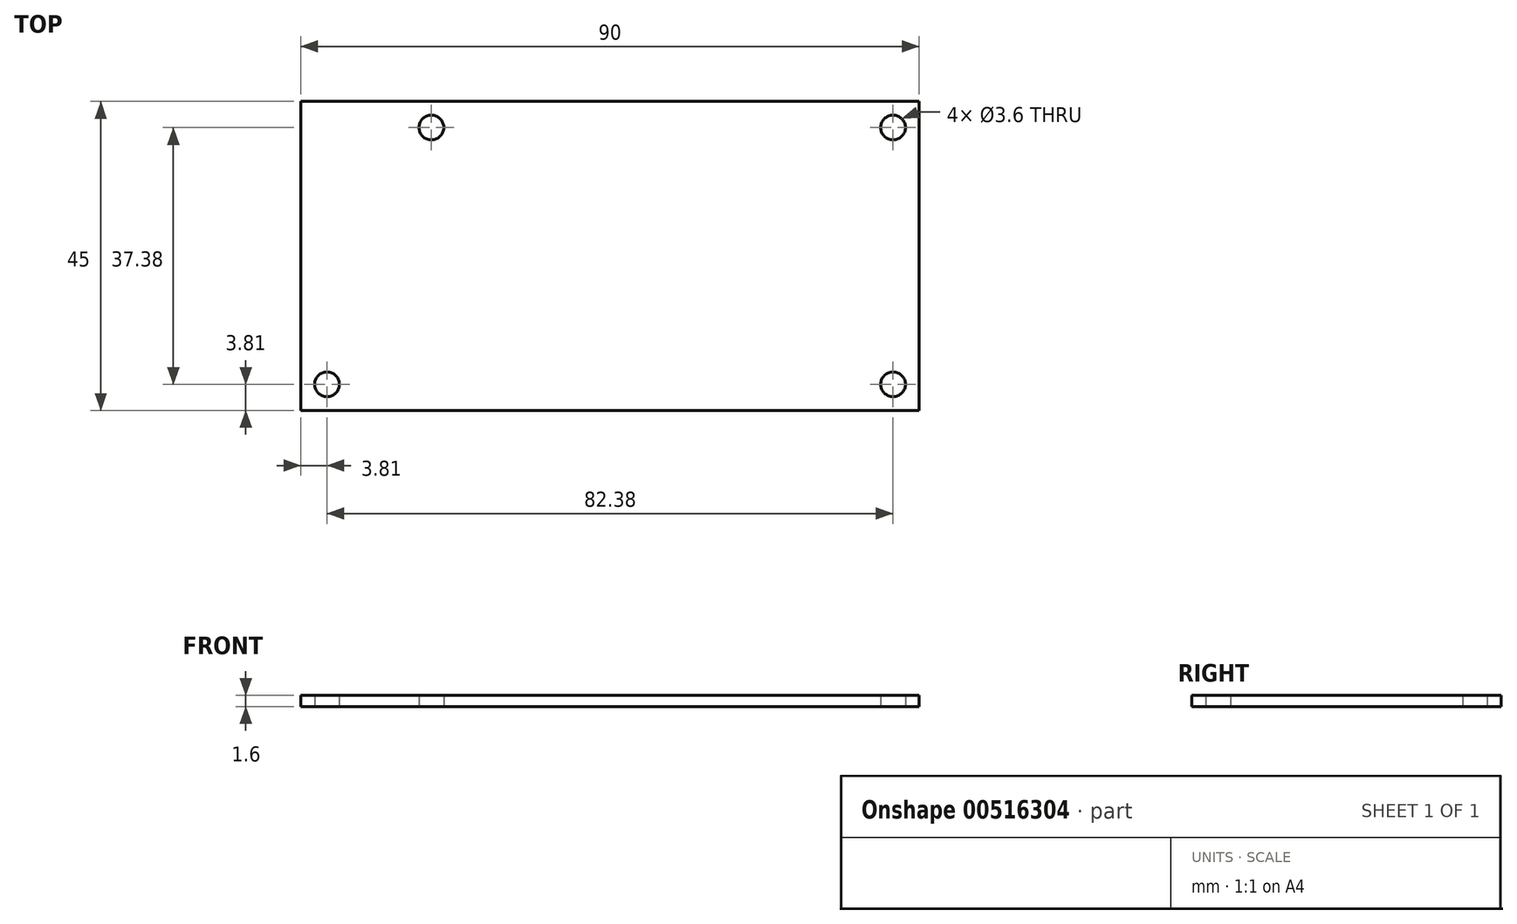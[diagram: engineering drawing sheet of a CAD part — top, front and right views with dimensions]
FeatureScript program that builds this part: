
annotation { "Feature Type Name" : "Feature", "Feature Type Description" : "" }
export const myFeature = defineFeature(function(context is Context, id is Id, definition is map)
    precondition{}
    {
        {
            var Q0;
            Q0=qCreatedBy(makeId("Top.planeOp"),FACE);
            var sketch = newSketch(context, id + "F0", { "sketchPlane" : qUnion([Q0])});
            skLineSegment(sketch, "E0.bottom", {"start": v(0, 0) * mm, "end": v(90, 0) * mm});
            skLineSegment(sketch, "E0.top", {"start": v(0, 45) * mm, "end": v(90, 45) * mm});
            skLineSegment(sketch, "E0.left", {"start": v(0, 0) * mm, "end": v(0, 45) * mm});
            skLineSegment(sketch, "E0.right", {"start": v(90, 0) * mm, "end": v(90, 45) * mm});
            skLineSegment(sketch, "E1", {"start": v(19, 41.19) * mm, "end": v(86.19, 41.19) * mm, "construction": true});
            skLineSegment(sketch, "E2", {"start": v(3.8, 3.81) * mm, "end": v(86.19, 3.81) * mm, "construction": true});
            skSolve(sketch);
        }
        {
            var Q0;
            Q0=makeQuery(id+"F0.imprint","IMPRINT",FACE,{"disambiguationData":[TD([[makeQuery(id+"F0.imprint","IMPRINT",EDGE,{"derivedFrom":sQuery(id+"F0.wireOp",EDGE,"E0.bottom")}),1.0]])]});
            extrude(context, id + "F1", {"entities" : qUnion([Q0]), "depth" : 1.6 * mm});
        }
        {
            var Q0;
            Q0=sQuery(id+"F0.wireOp",VERTEX,"E1.start");
            var Q1;
            Q1=sQuery(id+"F0.wireOp",VERTEX,"E2.start");
            var Q2;
            Q2=sQuery(id+"F0.wireOp",VERTEX,"E1.end");
            var Q3;
            Q3=sQuery(id+"F0.wireOp",VERTEX,"E2.end");
            var Q4;
            Q4=makeQuery(id+"F1.opExtrude","SWEPT_BODY",BODY,{"disambiguationData":[OSD([sQuery(id+"F0.wireOp",EDGE,"E0.bottom"),sQuery(id+"F0.wireOp",EDGE,"E0.top"),sQuery(id+"F0.wireOp",EDGE,"E0.left"),sQuery(id+"F0.wireOp",EDGE,"E0.right")])]});
            hole(context, id + "F2", {"style" : HoleStyle.SIMPLE, "endStyle" : HoleEndStyle.THROUGH, "oppositeDirection" : true, "holeDiameter" : 3.6 * mm, "isTappedThrough" : true, "tappedDepth" : 12 * mm, "tapClearance" : 3, "locations" : qUnion([Q0, Q1, Q2, Q3]), "scope" : qUnion([Q4])});
        }
    });
